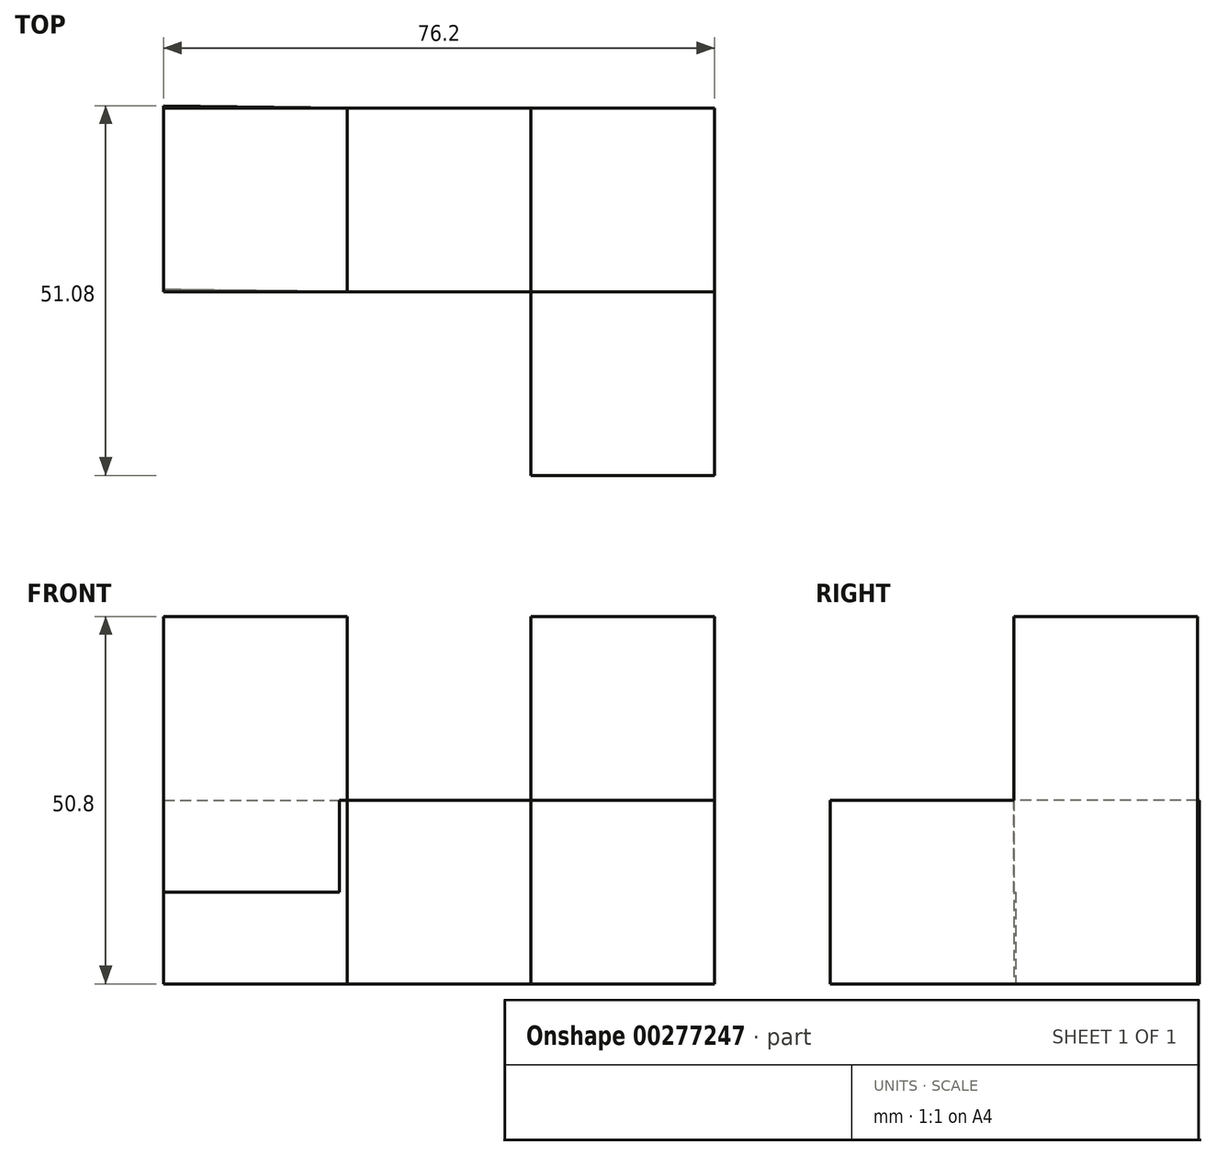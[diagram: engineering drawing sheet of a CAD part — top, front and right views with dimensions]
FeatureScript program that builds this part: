
annotation { "Feature Type Name" : "Feature", "Feature Type Description" : "" }
export const myFeature = defineFeature(function(context is Context, id is Id, definition is map)
    precondition{}
    {
        {
            var Q0;
            Q0=qCreatedBy(makeId("Top.planeOp"),FACE);
            var sketch = newSketch(context, id + "F0", { "sketchPlane" : qUnion([Q0])});
            skLineSegment(sketch, "E0", {"start": v(0, 0) * mm, "end": v(25.4, 0) * mm});
            skLineSegment(sketch, "E1", {"start": v(25.4, 0) * mm, "end": v(25.4, 25.4) * mm});
            skLineSegment(sketch, "E2", {"start": v(25.4, 25.4) * mm, "end": v(0, 25.4) * mm});
            skLineSegment(sketch, "E3", {"start": v(0, 25.4) * mm, "end": v(0, 0) * mm});
            skLineSegment(sketch, "E4", {"start": v(25.4, 25.4) * mm, "end": v(50.8, 25.4) * mm});
            skLineSegment(sketch, "E5", {"start": v(50.5, 25.4) * mm, "end": v(50.8, 0) * mm});
            skLineSegment(sketch, "E6", {"start": v(50.8, 0) * mm, "end": v(25.4, 0) * mm});
            skLineSegment(sketch, "E7", {"start": v(25.4, 0) * mm, "end": v(25.4, -25.4) * mm});
            skLineSegment(sketch, "E8", {"start": v(50.8, 0) * mm, "end": v(50.8, -25.4) * mm});
            skLineSegment(sketch, "E9", {"start": v(0.3, 25.39) * mm, "end": v(0, -0.01) * mm});
            skLineSegment(sketch, "E10", {"start": v(50.8, -25.4) * mm, "end": v(25.4, -25.4) * mm});
            skLineSegment(sketch, "E11", {"start": v(25.4, 25.4) * mm, "end": v(25.4, 0) * mm});
            skLineSegment(sketch, "E12", {"start": v(50.8, 25.4) * mm, "end": v(50.8, 0) * mm});
            skLineSegment(sketch, "E13", {"start": v(0, -0.01) * mm, "end": v(-25.4, 0.28) * mm});
            skLineSegment(sketch, "E14", {"start": v(-25.4, 0.28) * mm, "end": v(-25.4, 25.68) * mm});
            skLineSegment(sketch, "E15", {"start": v(-25.4, 25.68) * mm, "end": v(0, 25.4) * mm});
            skSolve(sketch);
        }
        {
            var Q0;
            Q0 = qSketchRegion(id + "F0", true);
            extrude(context, id + "F1", {"entities" : qUnion([Q0]), "endBound" : BoundingType.SYMMETRIC, "depth" : 25.4 * mm});
        }
        {
            var Q0;
            Q0=qCreatedBy(makeId("Top.planeOp"),FACE);
            var sketch = newSketch(context, id + "F2", { "sketchPlane" : qUnion([Q0])});
            skLineSegment(sketch, "E16.bottom", {"start": v(50.8, 25.4) * mm, "end": v(25.4, 25.4) * mm});
            skLineSegment(sketch, "E16.top", {"start": v(50.8, 0) * mm, "end": v(25.4, 0) * mm});
            skLineSegment(sketch, "E16.left", {"start": v(50.8, 25.4) * mm, "end": v(50.8, 0) * mm});
            skLineSegment(sketch, "E16.right", {"start": v(25.4, 25.4) * mm, "end": v(25.4, 0) * mm});
            skSolve(sketch);
        }
        {
            var Q0;
            Q0 = qSketchRegion(id + "F2", true);
            extrude(context, id + "F3", {"entities" : qUnion([Q0]), "operationType" : NewBodyOperationType.ADD, "depth" : 38.1 * mm});
        }
        {
            var Q0;
            Q0=qCreatedBy(makeId("Top.planeOp"),FACE);
            var sketch = newSketch(context, id + "F4", { "sketchPlane" : qUnion([Q0])});
            skLineSegment(sketch, "E17.bottom", {"start": v(0, 0) * mm, "end": v(-25.4, 0) * mm});
            skLineSegment(sketch, "E17.top", {"start": v(0, 25.4) * mm, "end": v(-25.4, 25.4) * mm});
            skLineSegment(sketch, "E17.left", {"start": v(0, 0) * mm, "end": v(0, 25.4) * mm});
            skLineSegment(sketch, "E17.right", {"start": v(-25.4, 0) * mm, "end": v(-25.4, 25.4) * mm});
            skSolve(sketch);
        }
        {
            var Q0;
            Q0 = qSketchRegion(id + "F4", true);
            extrude(context, id + "F5", {"entities" : qUnion([Q0]), "operationType" : NewBodyOperationType.ADD, "depth" : 38.1 * mm});
        }
    });
